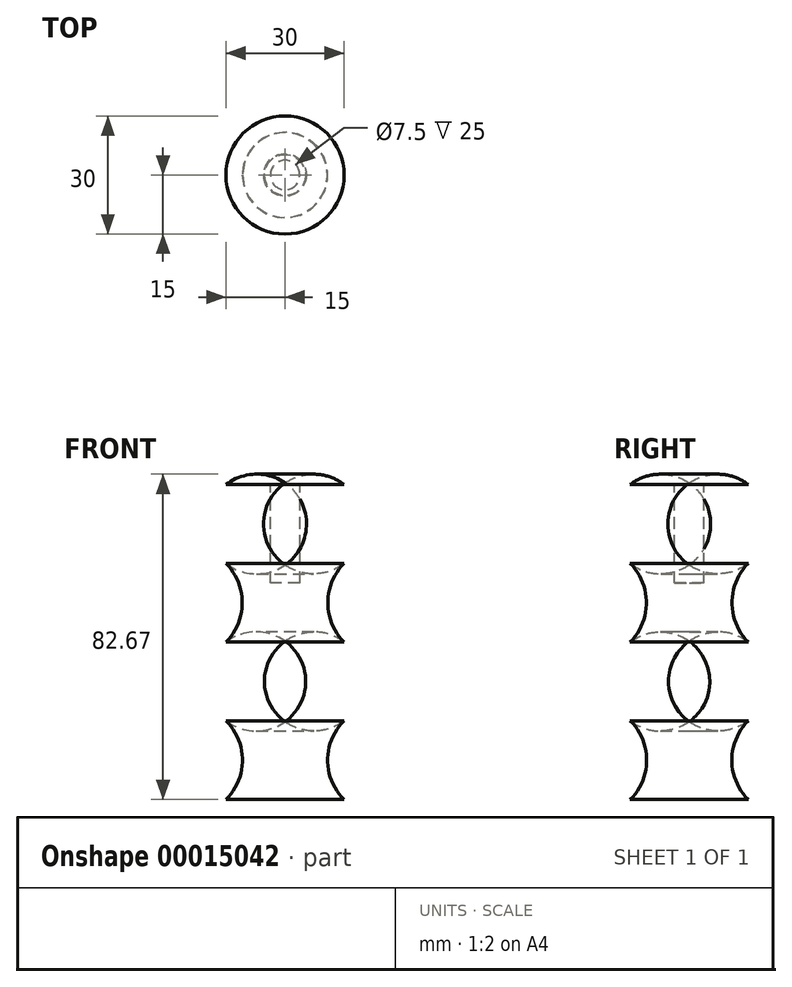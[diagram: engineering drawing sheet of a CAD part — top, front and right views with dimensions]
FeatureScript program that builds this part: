
annotation { "Feature Type Name" : "Feature", "Feature Type Description" : "" }
export const myFeature = defineFeature(function(context is Context, id is Id, definition is map)
    precondition{}
    {
        {
            var Q0;
            Q0=qCreatedBy(makeId("Front.planeOp"),FACE);
            var sketch = newSketch(context, id + "F0", { "sketchPlane" : qUnion([Q0])});
            skLineSegment(sketch, "E0", {"start": v(0, 0) * mm, "end": v(0, 80) * mm});
            skLineSegment(sketch, "E1.0", {"start": v(20, 0) * mm, "end": v(20, 80) * mm, "construction": true});
            skLineSegment(sketch, "E2", {"start": v(0, 80) * mm, "end": v(20, 80) * mm});
            skLineSegment(sketch, "E3.0", {"start": v(0, 70) * mm, "end": v(20, 70) * mm, "construction": true});
            skLineSegment(sketch, "E4.0", {"start": v(0, 60) * mm, "end": v(20, 60) * mm, "construction": true});
            skLineSegment(sketch, "E5.0", {"start": v(0, 40) * mm, "end": v(20, 40) * mm, "construction": true});
            skLineSegment(sketch, "E6.0", {"start": v(0, 20) * mm, "end": v(20, 20) * mm, "construction": true});
            skLineSegment(sketch, "E7.0", {"start": v(0, 0) * mm, "end": v(20, 0) * mm});
            skLineSegment(sketch, "E8.0", {"start": v(15, 0) * mm, "end": v(15, 80) * mm, "construction": true});
            skArc(sketch, "E9", {"start": v(15, 60) * mm, "mid": v(19.9, 70) * mm, "end": v(15, 80) * mm});
            skArc(sketch, "E10", {"start": v(15, 60) * mm, "mid": v(10.87, 50) * mm, "end": v(15, 40) * mm});
            skArc(sketch, "E11", {"start": v(15, 20) * mm, "mid": v(19.94, 30) * mm, "end": v(15, 40) * mm});
            skArc(sketch, "E12", {"start": v(15, 20) * mm, "mid": v(10.8, 10) * mm, "end": v(15, 0) * mm});
            skSolve(sketch);
        }
        {
            var Q0;
            {var subQ3=sQuery(id+"F0.wireOp",EDGE,"E0");Q0=makeQuery(id+"F0.imprint","IMPRINT",FACE,{"disambiguationData":[TD([[makeQuery(id+"F0.imprint","IMPRINT",EDGE,{"derivedFrom":subQ3}),-1.0]])]});}
            var Q1;
            Q1=sQuery(id+"F0.wireOp",EDGE,"E3.0");
            var Q2;
            Q2=sQuery(id+"F0.wireOp",EDGE,"E4.0");
            var Q3;
            Q3=sQuery(id+"F0.wireOp",EDGE,"E5.0");
            var Q4;
            Q4=sQuery(id+"F0.wireOp",EDGE,"E6.0");
            var Q5;
            Q5=sQuery(id+"F0.wireOp",EDGE,"E8.0");
            var Q6;
            Q6=sQuery(id+"F0.wireOp",EDGE,"E1.0");
            var Q7;
            Q7=sQuery(id+"F0.wireOp",EDGE,"E1.0");
            var Q8;
            Q8=sQuery(id+"F0.wireOp",EDGE,"E0");
            revolve(context, id + "F1", {"entities" : qUnion([Q0]), "surfaceEntities" : qUnion([Q1, Q2, Q3, Q4, Q5, Q6, Q7]), "axis" : qUnion([Q8]), "revolveType" : RevolveType.FULL});
        }
        {
            var Q0;
            Q0=makeQuery(id+"F1.opRevolve","SWEPT_FACE",FACE,{"disambiguationData":[OSD([sQuery(id+"F0.wireOp",EDGE,"E2")])]});
            var sketch = newSketch(context, id + "F2", { "sketchPlane" : qUnion([Q0])});
            skCircle(sketch, "E13", {"center": v(0, 0) * mm, "radius": 3.75 * mm});
            skSolve(sketch);
        }
        {
            var Q0;
            Q0 = qSketchRegion(id + "F2", true);
            extrude(context, id + "F3", {"entities" : qUnion([Q0]), "operationType" : NewBodyOperationType.REMOVE, "oppositeDirection" : true, "depth" : 25 * mm});
        }
    });
